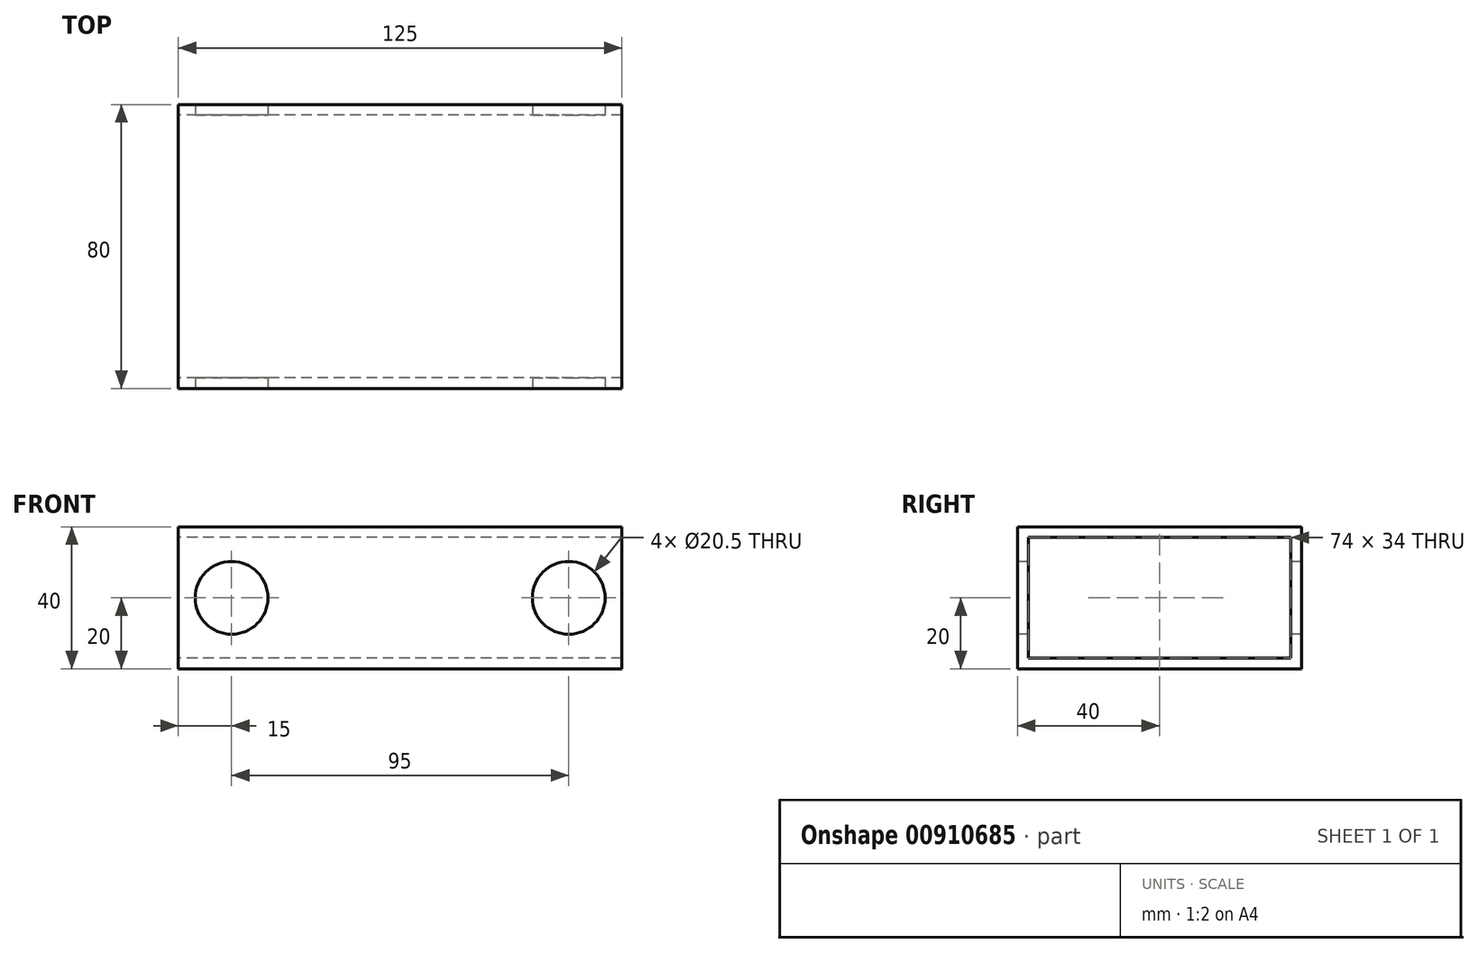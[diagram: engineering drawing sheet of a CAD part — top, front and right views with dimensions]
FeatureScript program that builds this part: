
annotation { "Feature Type Name" : "Feature", "Feature Type Description" : "" }
export const myFeature = defineFeature(function(context is Context, id is Id, definition is map)
    precondition{}
    {
        {
            var Q0;
            Q0=qCreatedBy(makeId("Right.planeOp"),FACE);
            var sketch = newSketch(context, id + "F0", { "sketchPlane" : qUnion([Q0])});
            skLineSegment(sketch, "E0.bottom", {"start": v(0, 0) * mm, "end": v(80, 0) * mm});
            skLineSegment(sketch, "E0.top", {"start": v(0, 40) * mm, "end": v(80, 40) * mm});
            skLineSegment(sketch, "E0.left", {"start": v(0, 0) * mm, "end": v(0, 40) * mm});
            skLineSegment(sketch, "E0.right", {"start": v(80, 0) * mm, "end": v(80, 40) * mm});
            skSolve(sketch);
        }
        {
            var Q0;
            Q0 = qSketchRegion(id + "F0", true);
            extrude(context, id + "F1", {"entities" : qUnion([Q0]), "depth" : 125 * mm, "offsetDistance" : 25 * mm});
        }
        {
            var Q0;
            Q0=makeQuery(id+"F1.opExtrude","CAP_FACE",FACE,{"disambiguationData":[OSD([sQuery(id+"F0.wireOp",EDGE,"E0.bottom"),sQuery(id+"F0.wireOp",EDGE,"E0.top"),sQuery(id+"F0.wireOp",EDGE,"E0.left"),sQuery(id+"F0.wireOp",EDGE,"E0.right")])],"isStart":false});
            var Q1;
            Q1=makeQuery(id+"F1.opExtrude","CAP_FACE",FACE,{"disambiguationData":[OSD([sQuery(id+"F0.wireOp",EDGE,"E0.bottom"),sQuery(id+"F0.wireOp",EDGE,"E0.top"),sQuery(id+"F0.wireOp",EDGE,"E0.left"),sQuery(id+"F0.wireOp",EDGE,"E0.right")])],"isStart":true});
            shell(context, id + "F2", {"entities" : qUnion([Q0, Q1]), "thickness" : 3 * mm});
        }
        {
            var Q0;
            Q0=makeQuery(id+"F1.opExtrude","SWEPT_FACE",FACE,{"disambiguationData":[OSD([sQuery(id+"F0.wireOp",EDGE,"E0.left")])]});
            var sketch = newSketch(context, id + "F3", { "sketchPlane" : qUnion([Q0])});
            skLineSegment(sketch, "E1", {"start": v(-8.5, 20) * mm, "end": v(143.17, 20) * mm, "construction": true});
            skCircle(sketch, "E2", {"center": v(15, 20) * mm, "radius": 10.25 * mm});
            skCircle(sketch, "E3", {"center": v(110, 20) * mm, "radius": 10.25 * mm});
            skSolve(sketch);
        }
        {
            var Q0;
            Q0 = qSketchRegion(id + "F3", true);
            extrude(context, id + "F4", {"entities" : qUnion([Q0]), "operationType" : NewBodyOperationType.REMOVE, "endBound" : BoundingType.THROUGH_ALL, "oppositeDirection" : true, "depth" : 25 * mm, "offsetDistance" : 25 * mm});
        }
    });
